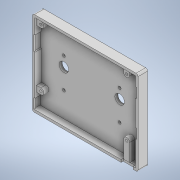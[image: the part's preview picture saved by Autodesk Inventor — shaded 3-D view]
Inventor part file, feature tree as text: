
AUTODESK INVENTOR PART (.ipt)
format: ipt  version: 2021 (Build 250183000, 183)  size: 384,512 bytes
history: native  units: mm
features: extrude x10, sketch x8, reference x3, projected_geometry x2, other x2, plane x1, fillet x1
ambient origin geometry x8: Origin, YZ Plane, XZ Plane, XY Plane, X Axis, Y Axis, Z Axis, Center Point
bodies: Body1 (feature_tree)
feature tree (27):
  plane  "Work Plane1"
  extrude  "Extrusion1"  Depth=2.9mm
  extrude  "Extrusion2"  Depth=2.9mm
  extrude  "Extrusion7"  Depth=3.0mm
  extrude  "Extrusion8"  Depth=3.0mm
  fillet  "Fillet1"  Radius=3.0mm
  extrude  "Extrusion9"  Depth=6.0mm
  extrude  "Extrusion10"  Depth=6.0mm
  extrude  "Extrusion11"  Depth=6.0mm TaperAngle=0.0deg
  extrude  "Extrusion14"  Depth=3.0mm
  extrude  "Extrusion15"  Depth=3.0mm
  extrude  "Extrusion16"  Depth=3.0mm
  sketch  "Sketch1"  dims[d0=2.9mm d1=2.9mm]
  sketch  "Sketch2"  dims[d2=2.9mm d3=2.9mm]
  sketch  "Sketch10"  dims[d4=3.0mm d5=3.0mm]
  reference  "Reference1"
  reference  "Reference2"
  reference  "Reference3"
  sketch  "Sketch11"  dims[d6=3.0mm d7=3.0mm d8=3.0mm d9=0.0mm]
  projected_geometry  "Projected Loop3"
  sketch  "Sketch12"  dims[d10=6.0mm d11=6.0mm]
  projected_geometry  "Projected Loop4"
  sketch  "Sketch15"  dims[d12=6.0mm d13=6.0mm]
  sketch  "Sketch16"  dims[d14=5.0mm d15=0.0mm d42=6.0mm d43=6.0mm d44=0.0mm]
  sketch  "Sketch17"  dims[d45=3.0mm d46=3.0mm d47=3.0mm d48=3.0mm d49=6.57mm d50=0.0mm d67=0.5mm d68=0.5mm d69=0.5mm d70=0.5mm d71=2.0mm d72=2.0mm d73=10.0mm d74=0.0mm d75=15.0mm d76=15.0mm d77=25.0mm d78=10.0mm d79=2.0mm d80=2.0mm d81=1.5mm d82=0.0mm d83=10.0mm d84=10.0mm d85=25.0mm d86=10.0mm d87=2.0mm d88=2.0mm d89=1.5mm d90=0.0mm d95=1.0mm d96=1.0mm d97=1.0mm d98=1.0mm d99=2.0mm d100=0.0mm d101=2.4mm d102=2.4mm d103=2.4mm d104=2.4mm d105=2.0mm d106=0.0mm d108=9.534mm d109=10.0mm d110=0.0mm]
  other  "Assembly1"
  other  "jetson_connector_cover:1"
